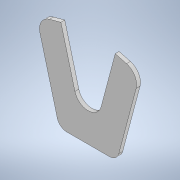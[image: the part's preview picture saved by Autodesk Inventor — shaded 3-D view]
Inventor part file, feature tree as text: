
AUTODESK INVENTOR PART (.ipt)
format: ipt  version: 2022.2 (Build 262287030, 287C)  size: 114,176 bytes
history: native  units: in
note: dims shown in document units (in); Inventor stores cm internally (conversion verified against a paired STEP export)
features: extrude x1, sketch x1
ambient origin geometry x8: Origin, YZ Plane, XZ Plane, XY Plane, X Axis, Y Axis, Z Axis, Center Point
bodies: Solid1 (feature_tree)
feature tree (2):
  extrude  "Extrusion1"  Depth=0.875in
  sketch  "Sketch1"  dims[d0=2.75in d1=0.875in d2=0.625in d3=1.375in d4=1.625in d5=2.25in d6=0.875in d7=0.25in d8=0.0in]
